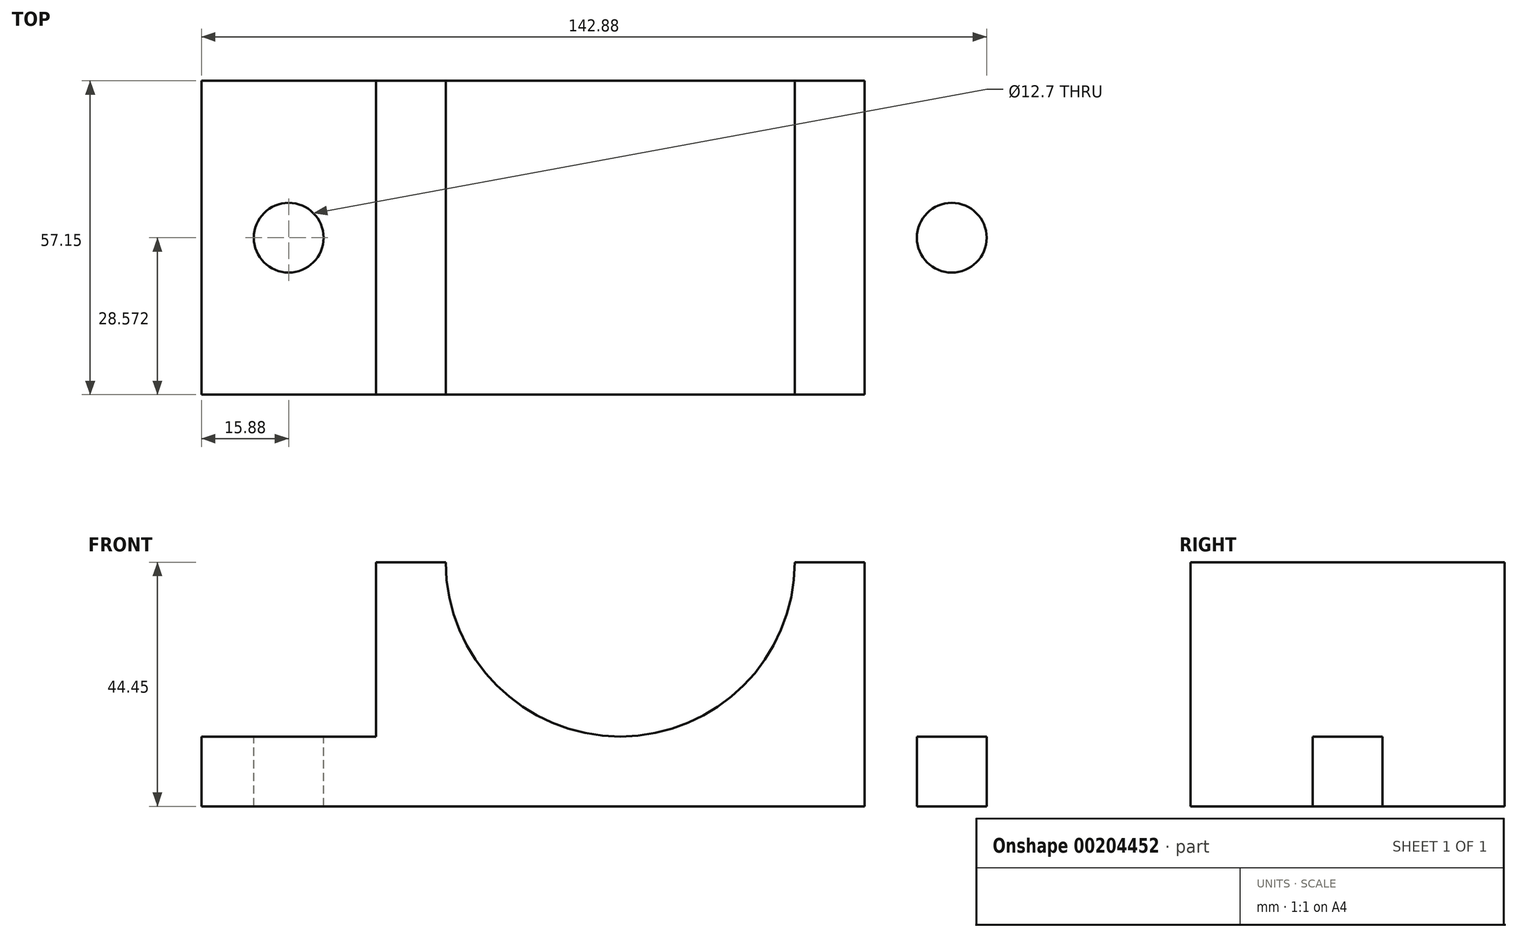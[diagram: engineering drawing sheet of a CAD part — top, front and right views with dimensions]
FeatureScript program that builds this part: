
annotation { "Feature Type Name" : "Feature", "Feature Type Description" : "" }
export const myFeature = defineFeature(function(context is Context, id is Id, definition is map)
    precondition{}
    {
        {
            var Q0;
            Q0=qCreatedBy(makeId("Top.planeOp"),FACE);
            var sketch = newSketch(context, id + "F0", { "sketchPlane" : qUnion([Q0])});
            skLineSegment(sketch, "E0.bottom", {"start": v(-77.92, 18.84) * mm, "end": v(74.48, 18.84) * mm});
            skLineSegment(sketch, "E0.top", {"start": v(-77.92, -38.31) * mm, "end": v(74.48, -38.31) * mm});
            skLineSegment(sketch, "E0.left", {"start": v(-77.92, 18.84) * mm, "end": v(-77.92, -38.31) * mm});
            skLineSegment(sketch, "E0.right", {"start": v(74.48, 18.84) * mm, "end": v(74.48, -38.31) * mm});
            skSolve(sketch);
        }
        {
            var Q0;
            Q0 = qSketchRegion(id + "F0", true);
            extrude(context, id + "F1", {"entities" : qUnion([Q0]), "depth" : 12.7 * mm});
        }
        {
            var Q0;
            Q0=makeQuery(id+"F1.opExtrude","CAP_FACE",FACE,{"disambiguationData":[OSD([sQuery(id+"F0.wireOp",EDGE,"E0.bottom"),sQuery(id+"F0.wireOp",EDGE,"E0.top"),sQuery(id+"F0.wireOp",EDGE,"E0.left"),sQuery(id+"F0.wireOp",EDGE,"E0.right")])],"isStart":false});
            var sketch = newSketch(context, id + "F2", { "sketchPlane" : qUnion([Q0])});
            skLineSegment(sketch, "E1", {"start": v(-77.92, 18.84) * mm, "end": v(-62.04, 18.84) * mm});
            skLineSegment(sketch, "E2", {"start": v(-77.92, 18.84) * mm, "end": v(-77.92, -9.74) * mm});
            skCircle(sketch, "E3", {"center": v(-62.04, -9.74) * mm, "radius": 6.35 * mm});
            skCircle(sketch, "E4.MirrorC", {"center": v(58.6, -9.74) * mm, "radius": 6.35 * mm});
            skLineSegment(sketch, "E5", {"start": v(74.48, 18.84) * mm, "end": v(42.73, 18.84) * mm});
            skLineSegment(sketch, "E6", {"start": v(42.73, 18.84) * mm, "end": v(42.73, -38.31) * mm});
            skLineSegment(sketch, "E7.MirrorCS", {"start": v(-46.17, 18.84) * mm, "end": v(-46.17, -38.31) * mm});
            skSolve(sketch);
        }
        {
            var Q0;
            Q0=makeQuery(id+"F2.imprint","IMPRINT",FACE,{"disambiguationData":[TD([[makeQuery(id+"F2.imprint","IMPRINT",EDGE,{"derivedFrom":sQuery(id+"F2.wireOp",EDGE,"E4.MirrorC")}),-1.0]])]});
            var Q1;
            Q1=makeQuery(id+"F2.imprint","IMPRINT",FACE,{"disambiguationData":[TD([[makeQuery(id+"F2.imprint","IMPRINT",EDGE,{"derivedFrom":sQuery(id+"F2.wireOp",EDGE,"E3")}),1.0]])]});
            extrude(context, id + "F3", {"entities" : qUnion([Q0, Q1]), "operationType" : NewBodyOperationType.REMOVE, "endBound" : BoundingType.THROUGH_ALL, "oppositeDirection" : true, "depth" : 25.4 * mm});
        }
        {
            var Q0;
            {var subQ0=sQuery(id+"F2.wireOp",EDGE,"E6");Q0=makeQuery(id+"F2.imprint","IMPRINT",FACE,{"disambiguationData":[TD([[makeQuery(id+"F2.imprint","IMPRINT",EDGE,{"derivedFrom":subQ0}),-1.0]])]});}
            extrude(context, id + "F4", {"entities" : qUnion([Q0]), "operationType" : NewBodyOperationType.ADD, "depth" : 31.75 * mm});
        }
        {
            var Q0;
            {var subQ0=sQuery(id+"F0.wireOp",EDGE,"E0.top");Q0=makeQuery(id+"F4.boolean.opBoolean","MERGE",FACE,{"derivedFrom":[makeQuery(id+"F1.opExtrude","SWEPT_FACE",FACE,{"disambiguationData":[OSD([subQ0])]}),makeQuery(id+"F4.opExtrude","SWEPT_FACE",FACE,{"disambiguationData":[OSD([subQ0])]})]});}
            var sketch = newSketch(context, id + "F5", { "sketchPlane" : qUnion([Q0])});
            skCircle(sketch, "E8", {"center": v(-1.72, 44.45) * mm, "radius": 31.75 * mm});
            skSolve(sketch);
        }
        {
            var Q0;
            {var subQ0=sQuery(id+"F5.wireOp",EDGE,"E8");var subQ1=makeQuery(id+"F4.opExtrude","CAP_EDGE",EDGE,{"disambiguationData":[OSD([sQuery(id+"F0.wireOp",EDGE,"E0.top")])],"isStart":false});var subQ2=makeQuery(id+"F5.imprint","INTERSECT",VERTEX,{"disambiguationData":[OD(0.0)],"derivedFrom":[subQ1,subQ0]});Q0=makeQuery(id+"F5.imprint","IMPRINT",FACE,{"disambiguationData":[TD([[makeQuery(id+"F5.imprint","IMPRINT",EDGE,{"disambiguationData":[TD([[subQ2,1.0]])],"derivedFrom":subQ0}),1.0]])]});}
            extrude(context, id + "F6", {"entities" : qUnion([Q0]), "operationType" : NewBodyOperationType.REMOVE, "endBound" : BoundingType.THROUGH_ALL, "oppositeDirection" : true, "depth" : 25.4 * mm});
        }
    });
